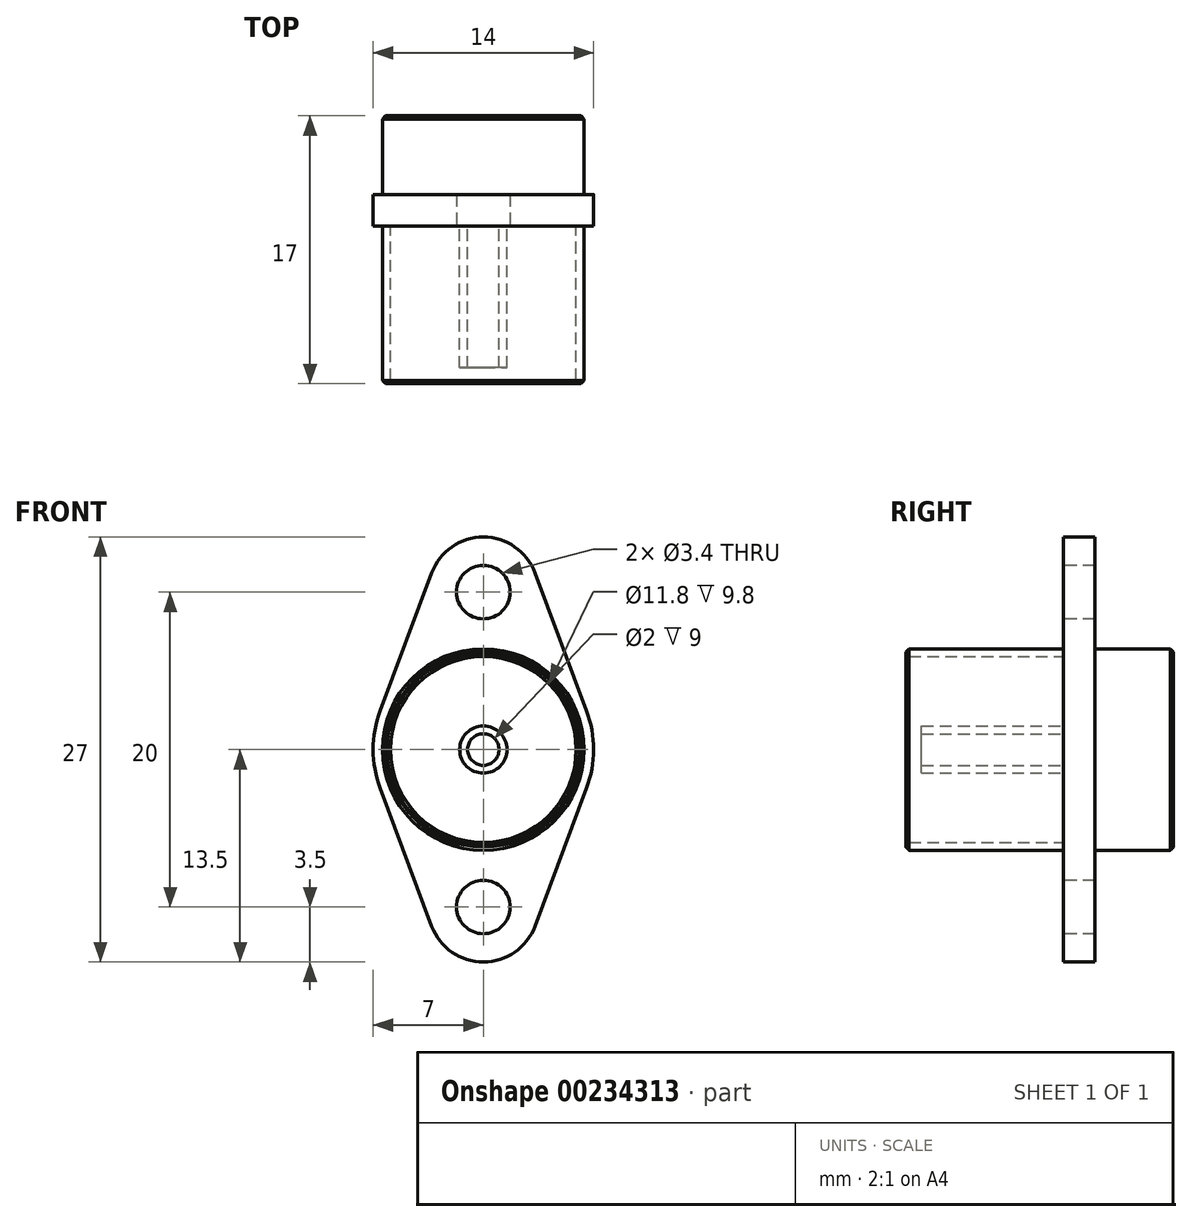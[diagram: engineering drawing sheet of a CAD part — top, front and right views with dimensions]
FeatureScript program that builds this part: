
annotation { "Feature Type Name" : "Feature", "Feature Type Description" : "" }
export const myFeature = defineFeature(function(context is Context, id is Id, definition is map)
    precondition{}
    {
        {
            var Q0;
            Q0=qCreatedBy(makeId("Front.planeOp"),FACE);
            var sketch = newSketch(context, id + "F0", { "sketchPlane" : qUnion([Q0])});
            skCircle(sketch, "E0", {"center": v(0, 10) * mm, "radius": 1.7 * mm});
            skCircle(sketch, "E1", {"center": v(0, -10) * mm, "radius": 1.7 * mm});
            skLineSegment(sketch, "E2", {"start": v(0, 10) * mm, "end": v(0, -10) * mm, "construction": true});
            skPoint(sketch, "E3", {"position": v(0, 0) * mm});
            skCircle(sketch, "E4", {"center": v(0, 0) * mm, "radius": 6.4 * mm});
            skArc(sketch, "E5", {"start": v(3.28, 11.23) * mm, "mid": v(0, 13.5) * mm, "end": v(-3.28, 11.22) * mm});
            skArc(sketch, "E6", {"start": v(-3.28, -11.22) * mm, "mid": v(0, -13.5) * mm, "end": v(3.28, -11.23) * mm});
            skCircle(sketch, "E7", {"center": v(0, 0) * mm, "radius": 7 * mm});
            skLineSegment(sketch, "E8", {"start": v(-3.28, 11.22) * mm, "end": v(-6.56, 2.45) * mm});
            skLineSegment(sketch, "E9", {"start": v(3.28, 11.22) * mm, "end": v(6.56, 2.45) * mm});
            skLineSegment(sketch, "E10", {"start": v(-3.28, -11.23) * mm, "end": v(-6.56, -2.45) * mm});
            skLineSegment(sketch, "E11", {"start": v(3.28, -11.22) * mm, "end": v(6.56, -2.45) * mm});
            skCircle(sketch, "E12", {"center": v(0, 0) * mm, "radius": 5.9 * mm});
            skCircle(sketch, "E13", {"center": v(0, 0) * mm, "radius": 1.5 * mm});
            skCircle(sketch, "E14", {"center": v(0, 0) * mm, "radius": 1 * mm});
            skSolve(sketch);
        }
        {
            var Q0;
            Q0=makeQuery(id+"F0.imprint","IMPRINT",FACE,{"disambiguationData":[TD([[makeQuery(id+"F0.imprint","IMPRINT",EDGE,{"derivedFrom":sQuery(id+"F0.wireOp",EDGE,"E0")}),-1.0]])]});
            var Q1;
            Q1=makeQuery(id+"F0.imprint","IMPRINT",FACE,{"disambiguationData":[TD([[makeQuery(id+"F0.imprint","IMPRINT",EDGE,{"derivedFrom":sQuery(id+"F0.wireOp",EDGE,"E1")}),-1.0]])]});
            var Q2;
            Q2=makeQuery(id+"F0.imprint","IMPRINT",FACE,{"disambiguationData":[TD([[makeQuery(id+"F0.imprint","IMPRINT",EDGE,{"derivedFrom":sQuery(id+"F0.wireOp",EDGE,"E4")}),-1.0]])]});
            var Q3;
            Q3=makeQuery(id+"F0.imprint","IMPRINT",FACE,{"disambiguationData":[TD([[makeQuery(id+"F0.imprint","IMPRINT",EDGE,{"derivedFrom":sQuery(id+"F0.wireOp",EDGE,"E4")}),1.0]])]});
            var Q4;
            Q4=makeQuery(id+"F0.imprint","IMPRINT",FACE,{"disambiguationData":[TD([[makeQuery(id+"F0.imprint","IMPRINT",EDGE,{"derivedFrom":sQuery(id+"F0.wireOp",EDGE,"E12")}),1.0]])]});
            var Q5;
            Q5=makeQuery(id+"F0.imprint","IMPRINT",FACE,{"disambiguationData":[TD([[makeQuery(id+"F0.imprint","IMPRINT",EDGE,{"derivedFrom":sQuery(id+"F0.wireOp",EDGE,"E13")}),1.0]])]});
            var Q6;
            Q6=makeQuery(id+"F0.imprint","IMPRINT",FACE,{"disambiguationData":[TD([[makeQuery(id+"F0.imprint","IMPRINT",EDGE,{"derivedFrom":sQuery(id+"F0.wireOp",EDGE,"E14")}),1.0]])]});
            extrude(context, id + "F1", {"entities" : qUnion([Q0, Q1, Q2, Q3, Q4, Q5, Q6]), "oppositeDirection" : true, "depth" : 2 * mm});
        }
        {
            var Q0;
            Q0=makeQuery(id+"F0.imprint","IMPRINT",FACE,{"disambiguationData":[TD([[makeQuery(id+"F0.imprint","IMPRINT",EDGE,{"derivedFrom":sQuery(id+"F0.wireOp",EDGE,"E4")}),1.0]])]});
            var Q1;
            Q1=makeQuery(id+"F0.imprint","IMPRINT",FACE,{"disambiguationData":[TD([[makeQuery(id+"F0.imprint","IMPRINT",EDGE,{"derivedFrom":sQuery(id+"F0.wireOp",EDGE,"E12")}),1.0]])]});
            var Q2;
            Q2=makeQuery(id+"F0.imprint","IMPRINT",FACE,{"disambiguationData":[TD([[makeQuery(id+"F0.imprint","IMPRINT",EDGE,{"derivedFrom":sQuery(id+"F0.wireOp",EDGE,"E13")}),1.0]])]});
            var Q3;
            Q3=makeQuery(id+"F0.imprint","IMPRINT",FACE,{"disambiguationData":[TD([[makeQuery(id+"F0.imprint","IMPRINT",EDGE,{"derivedFrom":sQuery(id+"F0.wireOp",EDGE,"E14")}),1.0]])]});
            extrude(context, id + "F2", {"entities" : qUnion([Q0, Q1, Q2, Q3]), "operationType" : NewBodyOperationType.ADD, "oppositeDirection" : true, "depth" : 7 * mm});
        }
        {
            var Q0;
            Q0=makeQuery(id+"F0.imprint","IMPRINT",FACE,{"disambiguationData":[TD([[makeQuery(id+"F0.imprint","IMPRINT",EDGE,{"derivedFrom":sQuery(id+"F0.wireOp",EDGE,"E4")}),1.0]])]});
            extrude(context, id + "F3", {"entities" : qUnion([Q0]), "operationType" : NewBodyOperationType.ADD, "depth" : 10 * mm});
        }
        {
            var Q0;
            Q0=makeQuery(id+"F0.imprint","IMPRINT",FACE,{"disambiguationData":[TD([[makeQuery(id+"F0.imprint","IMPRINT",EDGE,{"derivedFrom":sQuery(id+"F0.wireOp",EDGE,"E13")}),1.0]])]});
            extrude(context, id + "F4", {"entities" : qUnion([Q0]), "operationType" : NewBodyOperationType.ADD, "offsetDistance" : 25 * mm, "depth" : 9 * mm});
        }
        {
            var Q0;
            Q0=sQuery(id+"F0.wireOp",EDGE,"E12");
            extrude(context, id + "F5", {"bodyType" : ToolBodyType.SURFACE, "surfaceEntities" : qUnion([Q0]), "depth" : 9 * mm});
        }
        {
            var Q0;
            Q0=makeQuery(id+"F3.opExtrude","CAP_EDGE",EDGE,{"disambiguationData":[OSD([sQuery(id+"F0.wireOp",EDGE,"E4")])],"isStart":false});
            var Q1;
            Q1=makeQuery(id+"F3.opExtrude","CAP_EDGE",EDGE,{"disambiguationData":[OSD([sQuery(id+"F0.wireOp",EDGE,"E12")])],"isStart":false});
            var Q2;
            Q2=makeQuery(id+"F2.opExtrude","CAP_EDGE",EDGE,{"disambiguationData":[OSD([sQuery(id+"F0.wireOp",EDGE,"E4")])],"isStart":false});
            chamfer(context, id + "F6", {"entities" : qUnion([Q0, Q1, Q2]), "width" : .2 * mm, "tangentPropagation" : true});
        }
    });
